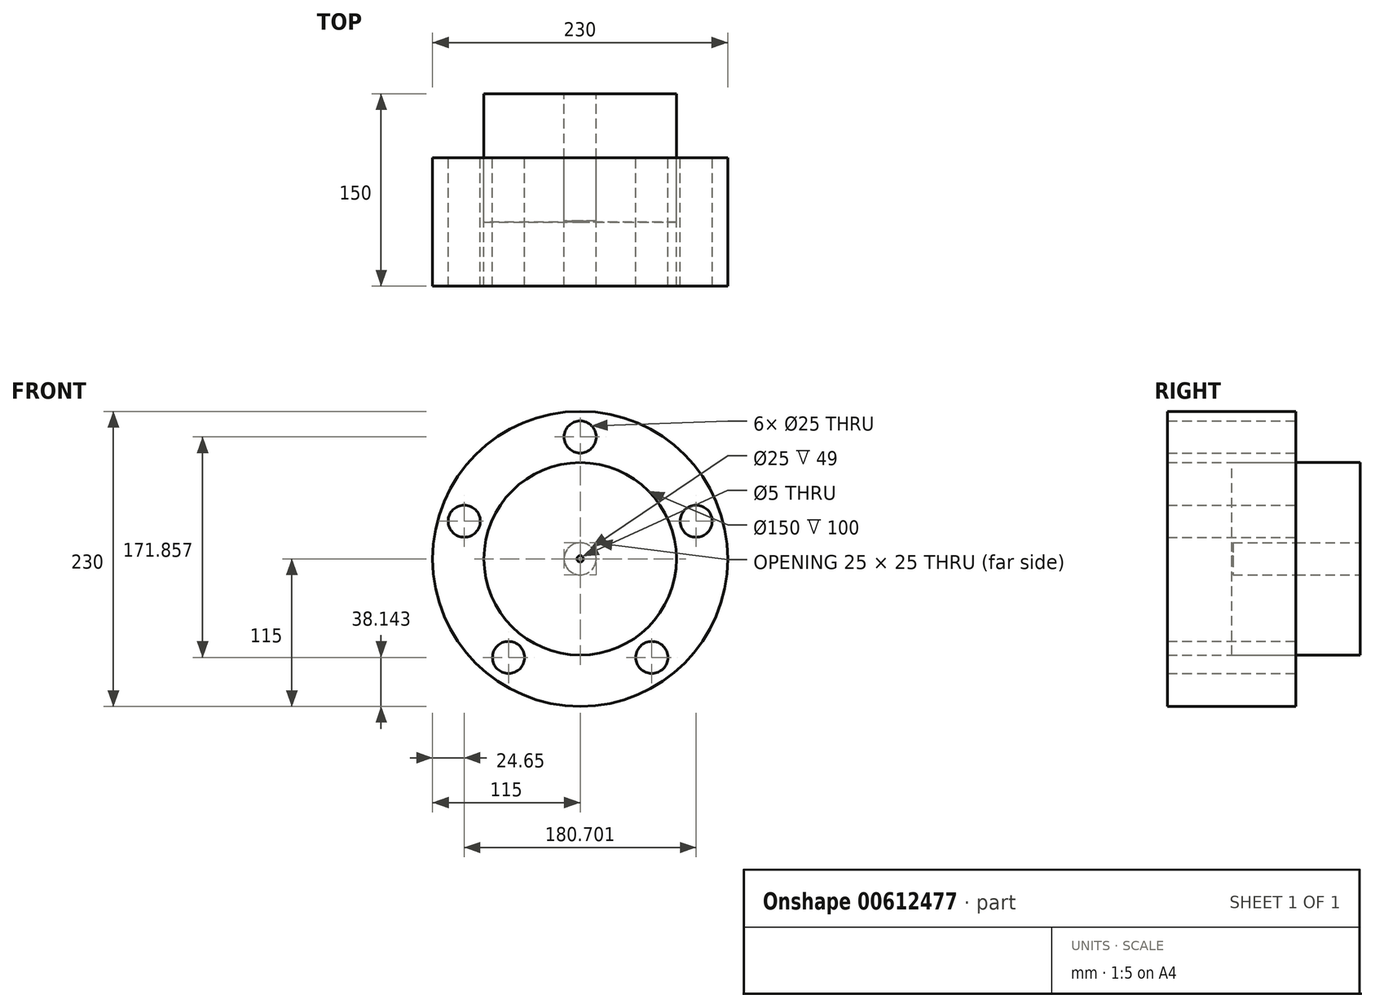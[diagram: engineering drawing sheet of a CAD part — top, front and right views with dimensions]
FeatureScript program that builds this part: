
annotation { "Feature Type Name" : "Feature", "Feature Type Description" : "" }
export const myFeature = defineFeature(function(context is Context, id is Id, definition is map)
    precondition{}
    {
        {
            var Q0;
            Q0=qCreatedBy(makeId("Front.planeOp"),FACE);
            var sketch = newSketch(context, id + "F0", { "sketchPlane" : qUnion([Q0])});
            skCircle(sketch, "E0", {"center": v(0, 0) * mm, "radius": 115 * mm});
            skCircle(sketch, "E1", {"center": v(0, 0) * mm, "radius": 75 * mm});
            skCircle(sketch, "E2", {"center": v(0, 95) * mm, "radius": 12.5 * mm});
            skCircle(sketch, "E3.1.0", {"center": v(-90.35, 29.36) * mm, "radius": 12.5 * mm});
            skCircle(sketch, "E3.2.0", {"center": v(-55.84, -76.86) * mm, "radius": 12.5 * mm});
            skCircle(sketch, "E4.1.3.0", {"center": v(55.84, -76.86) * mm, "radius": 12.5 * mm});
            skCircle(sketch, "E4.1.4.0", {"center": v(90.35, 29.36) * mm, "radius": 12.5 * mm});
            skSolve(sketch);
        }
        {
            var Q0;
            Q0=makeQuery(id+"F0.imprint","IMPRINT",FACE,{"disambiguationData":[TD([[makeQuery(id+"F0.imprint","IMPRINT",EDGE,{"derivedFrom":sQuery(id+"F0.wireOp",EDGE,"E0")}),1.0]])]});
            extrude(context, id + "F1", {"entities" : qUnion([Q0]), "depth" : 100 * mm, "offsetDistance" : 25 * mm});
        }
        {
            var Q0;
            Q0=makeQuery(id+"F0.imprint","IMPRINT",FACE,{"disambiguationData":[TD([[makeQuery(id+"F0.imprint","IMPRINT",EDGE,{"derivedFrom":sQuery(id+"F0.wireOp",EDGE,"E1")}),1.0]])]});
            var Q1;
            Q1=sQuery(id+"F0.wireOp",EDGE,"E1");
            extrude(context, id + "F2", {"entities" : qUnion([Q0]), "surfaceEntities" : qUnion([Q1]), "oppositeDirection" : true, "depth" : 50 * mm, "offsetDistance" : 25 * mm});
        }
        {
            var Q0;
            Q0=makeQuery(id+"F0.imprint","IMPRINT",FACE,{"disambiguationData":[TD([[makeQuery(id+"F0.imprint","IMPRINT",EDGE,{"derivedFrom":sQuery(id+"F0.wireOp",EDGE,"E1")}),1.0]])]});
            extrude(context, id + "F3", {"entities" : qUnion([Q0]), "depth" : 50 * mm, "offsetDistance" : 25 * mm});
        }
        {
            var Q0;
            Q0=makeQuery(id+"F2.opExtrude","CAP_FACE",FACE,{"disambiguationData":[OSD([sQuery(id+"F0.wireOp",EDGE,"E1")])],"isStart":false});
            var sketch = newSketch(context, id + "F4", { "sketchPlane" : qUnion([Q0])});
            skCircle(sketch, "E5", {"center": v(0, 0) * mm, "radius": 12.5 * mm});
            skSolve(sketch);
        }
        {
            var Q0;
            Q0 = qSketchRegion(id + "F4", true);
            extrude(context, id + "F5", {"entities" : qUnion([Q0]), "operationType" : NewBodyOperationType.REMOVE, "depth" : 25 * mm, "offsetDistance" : 25 * mm});
        }
        {
            var Q0;
            Q0=makeQuery(id+"F4.imprint","IMPRINT",FACE,{"disambiguationData":[TD([[makeQuery(id+"F4.imprint","IMPRINT",EDGE,{"derivedFrom":sQuery(id+"F4.wireOp",EDGE,"E5")}),1.0]])]});
            var Q1;
            Q1 = qSketchRegion(id + "F4", true);
            extrude(context, id + "F6", {"entities" : qUnion([Q0, Q1]), "operationType" : NewBodyOperationType.REMOVE, "oppositeDirection" : true, "depth" : 99 * mm, "offsetDistance" : 25 * mm});
        }
        {
            var Q0;
            Q0=makeQuery(id+"F4.imprint","IMPRINT",FACE,{"disambiguationData":[TD([[makeQuery(id+"F4.imprint","IMPRINT",EDGE,{"derivedFrom":sQuery(id+"F4.wireOp",EDGE,"E5")}),1.0]])]});
            var sketch = newSketch(context, id + "F7", { "sketchPlane" : qUnion([Q0])});
            skCircle(sketch, "E6", {"center": v(0, 0) * mm, "radius": 2.5 * mm});
            skSolve(sketch);
        }
        {
            var Q0;
            Q0 = qSketchRegion(id + "F7", true);
            extrude(context, id + "F8", {"entities" : qUnion([Q0]), "operationType" : NewBodyOperationType.REMOVE, "endBound" : BoundingType.THROUGH_ALL, "oppositeDirection" : true, "depth" : 25 * mm, "offsetDistance" : 25 * mm});
        }
    });
